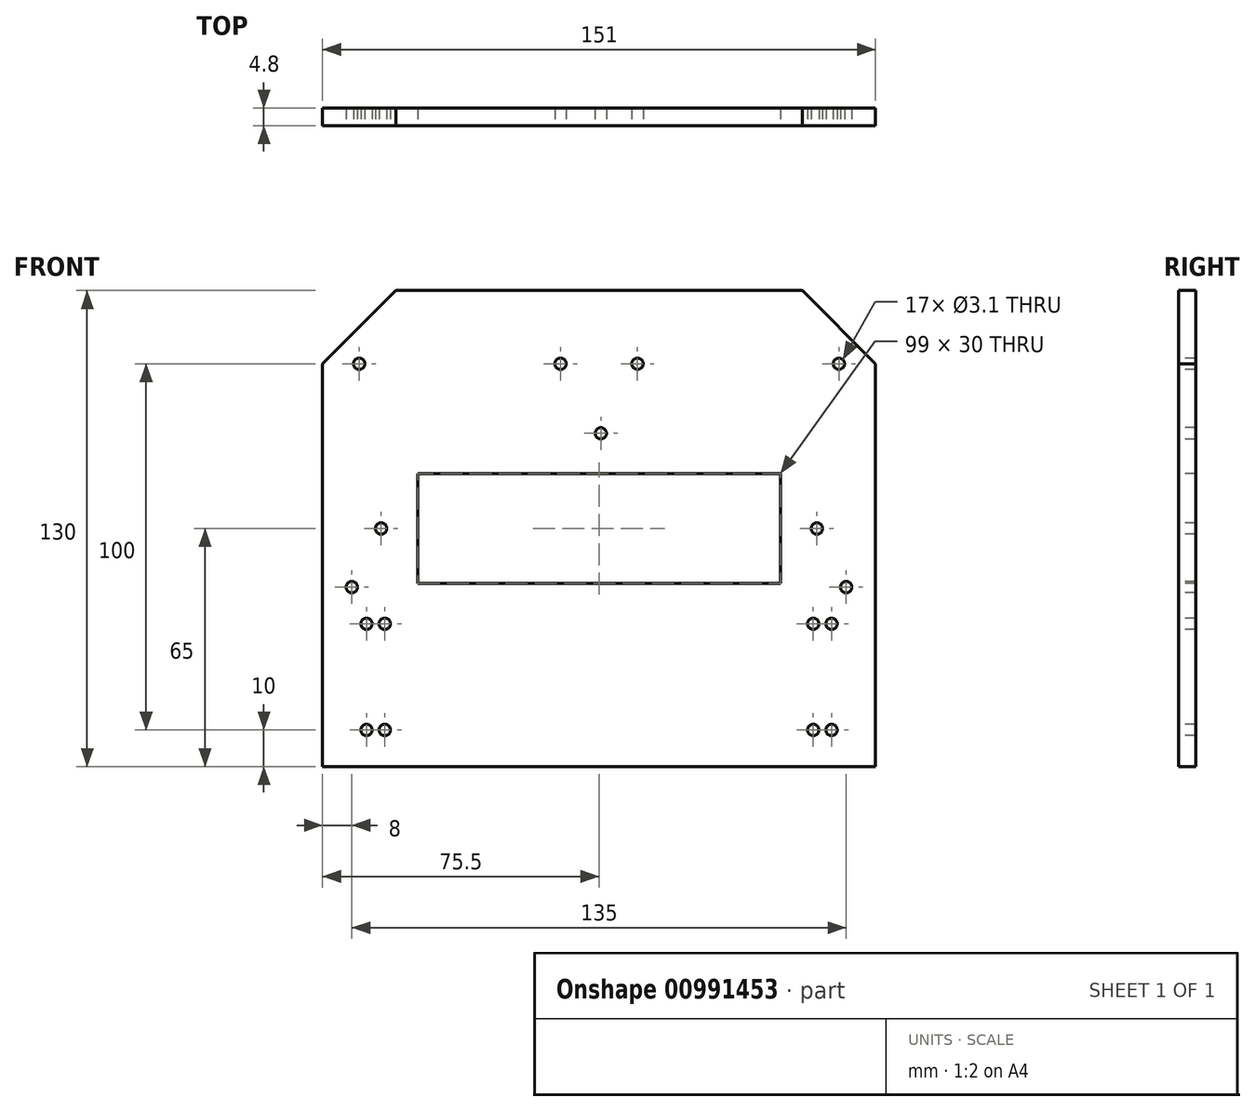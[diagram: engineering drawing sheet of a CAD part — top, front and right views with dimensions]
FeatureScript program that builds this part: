
annotation { "Feature Type Name" : "Feature", "Feature Type Description" : "" }
export const myFeature = defineFeature(function(context is Context, id is Id, definition is map)
    precondition{}
    {
        {
            var Q0;
            Q0=qCreatedBy(makeId("Front.planeOp"),FACE);
            var sketch = newSketch(context, id + "F0", { "sketchPlane" : qUnion([Q0])});
            skLineSegment(sketch, "E0.bottom", {"start": v(75.5, -65) * mm, "end": v(-75.5, -65) * mm});
            skLineSegment(sketch, "E0.top", {"start": v(75.5, 65) * mm, "end": v(-75.5, 65) * mm});
            skLineSegment(sketch, "E0.left", {"start": v(75.5, -65) * mm, "end": v(75.5, 65) * mm});
            skLineSegment(sketch, "E0.right", {"start": v(-75.5, -65) * mm, "end": v(-75.5, 65) * mm});
            skPoint(sketch, "E0.middle", {"position": v(0, 0) * mm});
            skSolve(sketch);
        }
        {
            var Q0;
            Q0=makeQuery(id+"F0.imprint","IMPRINT",FACE,{"disambiguationData":[TD([[makeQuery(id+"F0.imprint","IMPRINT",EDGE,{"derivedFrom":sQuery(id+"F0.wireOp",EDGE,"E0.bottom")}),-1.0]])]});
            extrude(context, id + "F1", {"entities" : qUnion([Q0]), "depth" : 4.8 * mm, "offsetDistance" : 25 * mm});
        }
        {
            var Q0;
            Q0=makeQuery(id+"F1.opExtrude","CAP_FACE",FACE,{"disambiguationData":[OSD([sQuery(id+"F0.wireOp",EDGE,"E0.bottom"),sQuery(id+"F0.wireOp",EDGE,"E0.top"),sQuery(id+"F0.wireOp",EDGE,"E0.left"),sQuery(id+"F0.wireOp",EDGE,"E0.right")])],"isStart":false});
            var sketch = newSketch(context, id + "F2", { "sketchPlane" : qUnion([Q0])});
            skLineSegment(sketch, "E1.bottom", {"start": v(49.5, -15) * mm, "end": v(-49.5, -15) * mm});
            skLineSegment(sketch, "E1.top", {"start": v(49.5, 15) * mm, "end": v(-49.5, 15) * mm});
            skLineSegment(sketch, "E1.left", {"start": v(49.5, -15) * mm, "end": v(49.5, 15) * mm});
            skLineSegment(sketch, "E1.right", {"start": v(-49.5, -15) * mm, "end": v(-49.5, 15) * mm});
            skPoint(sketch, "E1.middle", {"position": v(0, 0) * mm});
            skCircle(sketch, "E2", {"center": v(-59.5, 0) * mm, "radius": 1.55 * mm});
            skCircle(sketch, "E3", {"center": v(59.5, 0) * mm, "radius": 1.55 * mm});
            skCircle(sketch, "E4", {"center": v(-63.5, -55) * mm, "radius": 1.55 * mm});
            skCircle(sketch, "E5", {"center": v(63.5, -55) * mm, "radius": 1.55 * mm});
            skCircle(sketch, "E6", {"center": v(-58.5, -55) * mm, "radius": 1.55 * mm});
            skCircle(sketch, "E7", {"center": v(58.5, -55) * mm, "radius": 1.55 * mm});
            skCircle(sketch, "E8", {"center": v(-63.5, -26) * mm, "radius": 1.55 * mm});
            skCircle(sketch, "E9", {"center": v(-58.5, -26) * mm, "radius": 1.55 * mm});
            skCircle(sketch, "E10", {"center": v(63.5, -26) * mm, "radius": 1.55 * mm});
            skCircle(sketch, "E11", {"center": v(58.5, -26) * mm, "radius": 1.55 * mm});
            skCircle(sketch, "E12", {"center": v(65.5, 45) * mm, "radius": 1.55 * mm});
            skCircle(sketch, "E13", {"center": v(-65.5, 45) * mm, "radius": 1.55 * mm});
            skCircle(sketch, "E14", {"center": v(67.5, -16) * mm, "radius": 1.55 * mm});
            skCircle(sketch, "E15", {"center": v(-67.5, -16) * mm, "radius": 1.55 * mm});
            skCircle(sketch, "E16", {"center": v(10.5, 45) * mm, "radius": 1.55 * mm});
            skCircle(sketch, "E17", {"center": v(-10.5, 45) * mm, "radius": 1.55 * mm});
            skCircle(sketch, "E18", {"center": v(0.5, 26) * mm, "radius": 1.55 * mm});
            skSolve(sketch);
        }
        {
            var Q0;
            Q0 = qSketchRegion(id + "F2", true);
            extrude(context, id + "F3", {"entities" : qUnion([Q0]), "operationType" : NewBodyOperationType.REMOVE, "oppositeDirection" : true, "depth" : 4.8 * mm, "offsetDistance" : 25 * mm});
        }
        {
            var Q0;
            Q0=makeQuery(id+"F1.opExtrude","SWEPT_EDGE",EDGE,{"disambiguationData":[OSD([sQuery(id+"F0.wireOp",EDGE,"E0.top"),sQuery(id+"F0.wireOp",EDGE,"E0.right")])]});
            chamfer(context, id + "F4", {"entities" : qUnion([Q0]), "width" : 20 * mm, "tangentPropagation" : true});
        }
        {
            var Q0;
            Q0=makeQuery(id+"F1.opExtrude","SWEPT_EDGE",EDGE,{"disambiguationData":[OSD([sQuery(id+"F0.wireOp",EDGE,"E0.top"),sQuery(id+"F0.wireOp",EDGE,"E0.left")])]});
            chamfer(context, id + "F5", {"entities" : qUnion([Q0]), "width" : 20 * mm, "tangentPropagation" : true});
        }
    });
